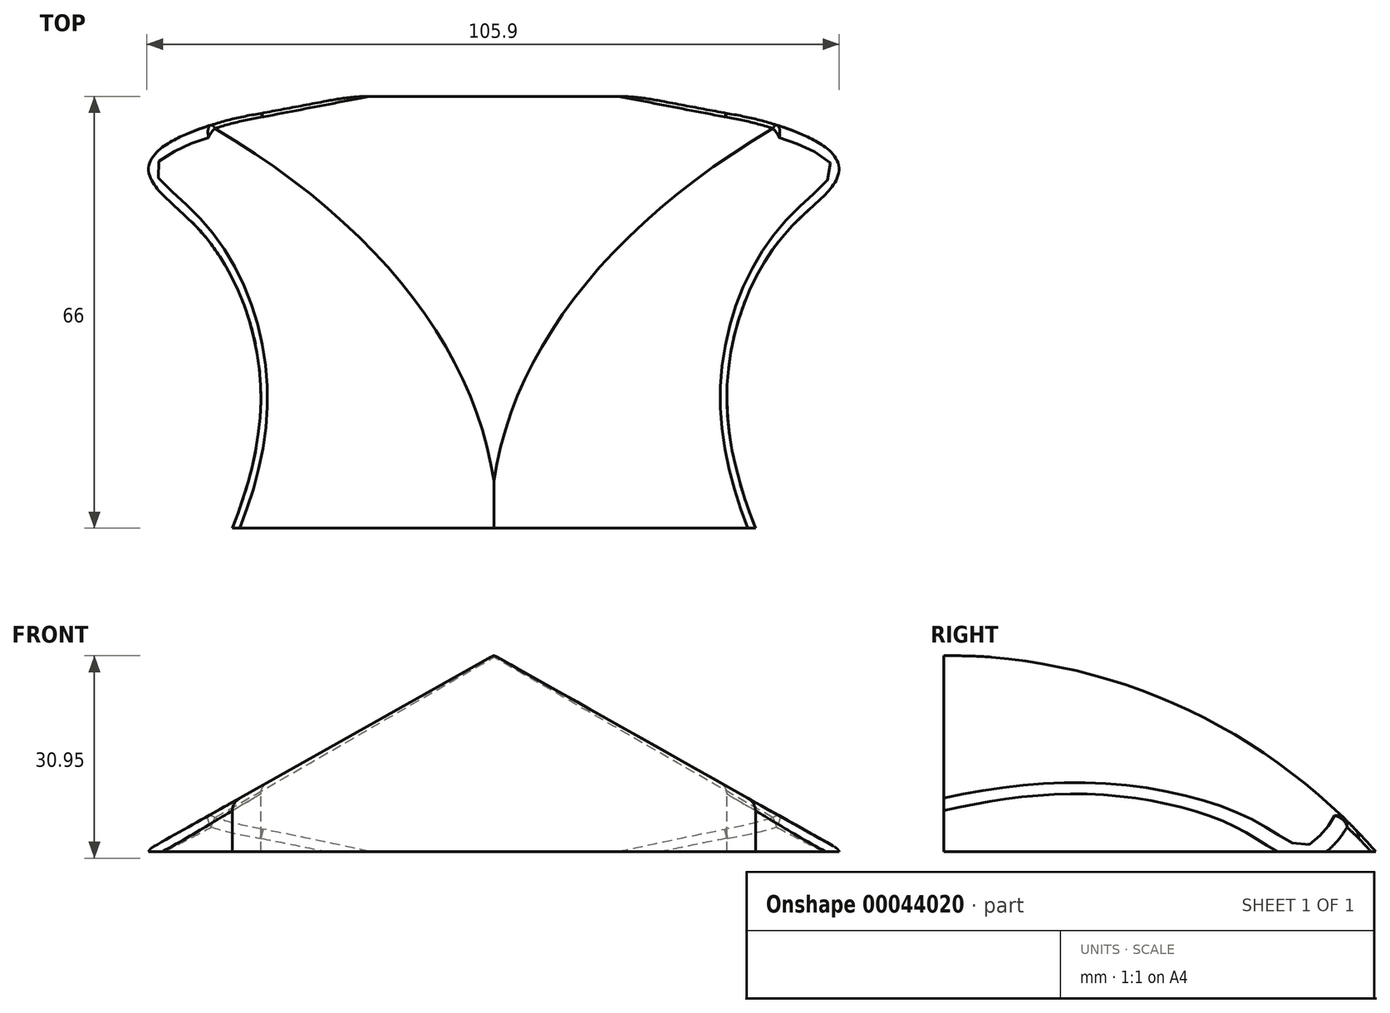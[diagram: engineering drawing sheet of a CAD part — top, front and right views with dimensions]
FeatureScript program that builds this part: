
annotation { "Feature Type Name" : "Feature", "Feature Type Description" : "" }
export const myFeature = defineFeature(function(context is Context, id is Id, definition is map)
    precondition{}
    {
        {
            var Q0;
            Q0=qCreatedBy(makeId("Top.planeOp"),FACE);
            cPlane(context, id + "F0", {"entities" : qUnion([Q0]), "cplaneType" : CPlaneType.OFFSET, "offset" : 30 * mm, "width" : 150 * mm, "height" : 150 * mm});
        }
        {
            var Q0;
            Q0=qCreatedBy(makeId("Top.planeOp"),FACE);
            var sketch = newSketch(context, id + "F1", { "sketchPlane" : qUnion([Q0])});
            skFitSpline(sketch, "E0", {"points": [v(-35.66, 21.54) * mm, v(-53.04, 13.52) * mm, v(-44.8, 3.49) * mm, v(-35.66, -19.99) * mm, v(-40, -41.85) * mm], "startDerivative": vector(-95.8, -14.73) * mm, "endDerivative": vector(-27.77, -69.38) * mm});
            skLineSegment(sketch, "E1", {"start": v(-40, -41.85) * mm, "end": v(0, -41.85) * mm});
            skLineSegment(sketch, "E2", {"start": v(-35.66, 21.54) * mm, "end": v(-21.83, 24.15) * mm});
            skLineSegment(sketch, "E3", {"start": v(-21.83, 24.15) * mm, "end": v(0, 24.15) * mm});
            skLineSegment(sketch, "E4.MirrorCS", {"start": v(35.66, 21.54) * mm, "end": v(21.83, 24.15) * mm});
            skLineSegment(sketch, "E5.MirrorCS", {"start": v(21.83, 24.15) * mm, "end": v(0, 24.15) * mm});
            skFitSpline(sketch, "E6.MirrorCS", {"points": [v(35.66, 21.54) * mm, v(53.04, 13.52) * mm, v(44.8, 3.49) * mm, v(35.66, -19.99) * mm, v(40, -41.85) * mm], "startDerivative": vector(95.8, -14.73) * mm, "endDerivative": vector(27.77, -69.38) * mm});
            skLineSegment(sketch, "E7.MirrorCS", {"start": v(40, -41.85) * mm, "end": v(0, -41.85) * mm});
            skLineSegment(sketch, "E8.bottom", {"start": v(70.01, -53.95) * mm, "end": v(-78.7, -53.95) * mm});
            skLineSegment(sketch, "E8.top", {"start": v(70.01, 37.7) * mm, "end": v(-78.7, 37.7) * mm});
            skLineSegment(sketch, "E8.left", {"start": v(70.01, -53.95) * mm, "end": v(70.01, 37.7) * mm});
            skLineSegment(sketch, "E8.right", {"start": v(-78.7, -53.95) * mm, "end": v(-78.7, 37.7) * mm});
            skSolve(sketch);
        }
        {
            var Q0;
            Q0=qCreatedBy(id+"F0.planeOp",FACE);
            var sketch = newSketch(context, id + "F2", { "sketchPlane" : qUnion([Q0])});
            skPoint(sketch, "E9", {"position": v(0, -41.85) * mm});
            skSolve(sketch);
        }
        {
            var Q0;
            Q0=qCreatedBy(makeId("Right.planeOp"),FACE);
            var sketch = newSketch(context, id + "F3", { "sketchPlane" : qUnion([Q0])});
            skLineSegment(sketch, "E10", {"start": v(-41.85, 0) * mm, "end": v(24.15, 0) * mm});
            skLineSegment(sketch, "E11", {"start": v(-41.85, 30) * mm, "end": v(-41.85, 0) * mm});
            skLineSegment(sketch, "E12", {"start": v(-41.85, 30) * mm, "end": v(24.15, 30) * mm, "construction": true});
            skArc(sketch, "E13", {"start": v(24.15, 0) * mm, "mid": v(-5.6, 22.15) * mm, "end": v(-41.85, 30) * mm});
            skSolve(sketch);
        }
        {
            var Q0;
            Q0=makeQuery(id+"F3.imprint","IMPRINT",FACE,{"disambiguationData":[TD([[makeQuery(id+"F3.imprint","IMPRINT",EDGE,{"derivedFrom":sQuery(id+"F3.wireOp",EDGE,"E10")}),1.0]])]});
            extrude(context, id + "F4", {"entities" : qUnion([Q0]), "depth" : 54 * mm, "hasSecondDirection" : true, "secondDirectionOppositeDirection" : true, "secondDirectionDepth" : 54 * mm});
        }
        {
            var Q0;
            Q0 = qSketchRegion(id + "F1", true);
            extrude(context, id + "F5", {"entities" : qUnion([Q0]), "operationType" : NewBodyOperationType.REMOVE, "depth" : 50 * mm});
        }
        {
            var Q0;
            Q0=makeQuery(id+"F4.opExtrude","SWEPT_FACE",FACE,{"disambiguationData":[OSD([sQuery(id+"F3.wireOp",EDGE,"E11")])]});
            var sketch = newSketch(context, id + "F6", { "sketchPlane" : qUnion([Q0])});
            skLineSegment(sketch, "E14", {"start": v(0, 30) * mm, "end": v(-53.35, 0) * mm});
            skLineSegment(sketch, "E15", {"start": v(-53.35, 0) * mm, "end": v(-53.35, 30) * mm});
            skLineSegment(sketch, "E16", {"start": v(0, 30) * mm, "end": v(-53.35, 30) * mm});
            skLineSegment(sketch, "E17.MirrorCS", {"start": v(0, 30) * mm, "end": v(53.35, 0) * mm});
            skLineSegment(sketch, "E18.MirrorCS", {"start": v(0, 30) * mm, "end": v(53.35, 30) * mm});
            skLineSegment(sketch, "E19.MirrorCS", {"start": v(53.35, 0) * mm, "end": v(53.35, 30) * mm});
            skSolve(sketch);
        }
        {
            var Q0;
            Q0 = qSketchRegion(id + "F6", true);
            extrude(context, id + "F7", {"entities" : qUnion([Q0]), "operationType" : NewBodyOperationType.REMOVE, "oppositeDirection" : true, "depth" : 100 * mm});
        }
        {
            var Q0;
            Q0=makeQuery(id+"F7.boolean.opBoolean","INTERSECT",EDGE,{"derivedFrom":[makeQuery(id+"F5.boolean.opBoolean","COPY",FACE,{"derivedFrom":makeQuery(id+"F5.opExtrude","SWEPT_FACE",FACE,{"disambiguationData":[OSD([sQuery(id+"F1.wireOp",EDGE,"E0")])]})}),makeQuery(id+"F7.opExtrude","SWEPT_FACE",FACE,{"disambiguationData":[OSD([sQuery(id+"F6.wireOp",EDGE,"E14")])]})]});
            var Q1;
            Q1=makeQuery(id+"F7.boolean.opBoolean","INTERSECT",EDGE,{"derivedFrom":[makeQuery(id+"F4.opExtrude","SWEPT_FACE",FACE,{"disambiguationData":[OSD([sQuery(id+"F3.wireOp",EDGE,"E13")])]}),makeQuery(id+"F7.opExtrude","SWEPT_FACE",FACE,{"disambiguationData":[OSD([sQuery(id+"F6.wireOp",EDGE,"E14")])]})]});
            var Q2;
            Q2=makeQuery(id+"F7.boolean.opBoolean","INTERSECT",EDGE,{"derivedFrom":[makeQuery(id+"F4.opExtrude","SWEPT_FACE",FACE,{"disambiguationData":[OSD([sQuery(id+"F3.wireOp",EDGE,"E13")])]}),makeQuery(id+"F7.opExtrude","SWEPT_FACE",FACE,{"disambiguationData":[OSD([sQuery(id+"F6.wireOp",EDGE,"E17.MirrorCS")])]})]});
            var Q3;
            Q3=makeQuery(id+"F7.boolean.opBoolean","INTERSECT",EDGE,{"derivedFrom":[makeQuery(id+"F5.boolean.opBoolean","COPY",FACE,{"derivedFrom":makeQuery(id+"F5.opExtrude","SWEPT_FACE",FACE,{"disambiguationData":[OSD([sQuery(id+"F1.wireOp",EDGE,"E6.MirrorCS")])]})}),makeQuery(id+"F7.opExtrude","SWEPT_FACE",FACE,{"disambiguationData":[OSD([sQuery(id+"F6.wireOp",EDGE,"E17.MirrorCS")])]})]});
            var Q4;
            Q4=makeQuery(id+"F5.boolean.opBoolean","INTERSECT",EDGE,{"derivedFrom":[makeQuery(id+"F4.opExtrude","SWEPT_FACE",FACE,{"disambiguationData":[OSD([sQuery(id+"F3.wireOp",EDGE,"E13")])]}),makeQuery(id+"F5.opExtrude","SWEPT_FACE",FACE,{"disambiguationData":[OSD([sQuery(id+"F1.wireOp",EDGE,"E0")])]})]});
            var Q5;
            Q5=makeQuery(id+"F5.boolean.opBoolean","INTERSECT",EDGE,{"derivedFrom":[makeQuery(id+"F4.opExtrude","SWEPT_FACE",FACE,{"disambiguationData":[OSD([sQuery(id+"F3.wireOp",EDGE,"E13")])]}),makeQuery(id+"F5.opExtrude","SWEPT_FACE",FACE,{"disambiguationData":[OSD([sQuery(id+"F1.wireOp",EDGE,"E2")])]})]});
            var Q6;
            Q6=makeQuery(id+"F5.boolean.opBoolean","INTERSECT",EDGE,{"derivedFrom":[makeQuery(id+"F4.opExtrude","SWEPT_FACE",FACE,{"disambiguationData":[OSD([sQuery(id+"F3.wireOp",EDGE,"E13")])]}),makeQuery(id+"F5.opExtrude","SWEPT_FACE",FACE,{"disambiguationData":[OSD([sQuery(id+"F1.wireOp",EDGE,"E6.MirrorCS")])]})]});
            var Q7;
            Q7=makeQuery(id+"F5.boolean.opBoolean","INTERSECT",EDGE,{"derivedFrom":[makeQuery(id+"F4.opExtrude","SWEPT_FACE",FACE,{"disambiguationData":[OSD([sQuery(id+"F3.wireOp",EDGE,"E13")])]}),makeQuery(id+"F5.opExtrude","SWEPT_FACE",FACE,{"disambiguationData":[OSD([sQuery(id+"F1.wireOp",EDGE,"E4.MirrorCS")])]})]});
            var Q8;
            Q8=makeQuery(id+"F5.boolean.opBoolean","COPY",EDGE,{"derivedFrom":makeQuery(id+"F5.opExtrude","SWEPT_EDGE",EDGE,{"disambiguationData":[OSD([sQuery(id+"F1.wireOp",EDGE,"E4.MirrorCS"),sQuery(id+"F1.wireOp",EDGE,"E6.MirrorCS")])]})});
            var Q9;
            Q9=makeQuery(id+"F5.boolean.opBoolean","COPY",EDGE,{"derivedFrom":makeQuery(id+"F5.opExtrude","SWEPT_EDGE",EDGE,{"disambiguationData":[OSD([sQuery(id+"F1.wireOp",EDGE,"E0"),sQuery(id+"F1.wireOp",EDGE,"E2")])]})});
            fillet(context, id + "F8", {"entities" : qUnion([Q0, Q1, Q2, Q3, Q4, Q5, Q6, Q7, Q8, Q9]), "radius" : 2 * mm, "tangentPropagation" : true, "allowEdgeOverflow" : false});
        }
    });
